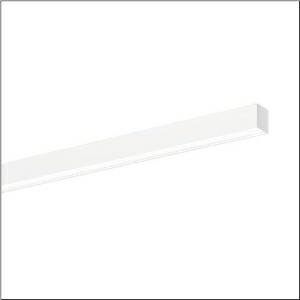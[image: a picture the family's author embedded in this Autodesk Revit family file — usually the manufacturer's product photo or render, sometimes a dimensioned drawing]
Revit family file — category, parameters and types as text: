
# Revit family: silica_r__21_51mx23db35wb_106f
name_source: partatom
category: Lighting Fixtures
units: mm (PartAtom-declared; Revit-internal decimal feet)

## family parameters
Cut with Voids When Loaded = No
Host = Face
Light Source = No
Part Type = Normal
Room Calculation Point = No
Round Connector Dimension = Use Diameter
Shared = No

## types (1)
- --- (1 x LED, 4100 lm, 30.1 W, 3000K)
    Apparent Load = 30 VA
    CIE Flux Codes = 78 96 99 100 100
    Color Rendering = 80
    Color Temperature = 3000K
    Default Elevation = 1800 mm
    Description = Silica® 21, office luminaire, primary optical cover: prismatic diffuser, of PMMA, CAT 2 (L<= 3000cd/m²), light emission: direct distribution, primary light characteristic: symmetric, installation type: surface-mounted, LED, rated luminous flux: 4.100lm, luminous efficacy: 136lm/W, light colour: 830, colour temperature: 3000K, control gear: DALI 2, with terminal, 3+2-pole, max. 2.5mm², mains connection: 220..240V, AC, 50/60Hz, rated input power: 30.1W, luminaire housing, of aluminium, traffic white (RAL 9016), length: 1.504mm, width: 53mm, height: 53mm, protection rating (complete): IP20, insulation class (complete): insulation class I (protective earthing), certification: CE, permissible operating ambient temperature: 0..+35°C, standard: EN 50419, packaging unit: 1 piece
    Height = 53 mm
    Lamp = 1 x LED
    Lamp Light Flux = 4100 lm
    Lamp Power = 30.1 W
    Lamp count = 1
    Length = 1504 mm
    Luminous efficacy = 136 lm/W
    Manufacturer = Siteco
    ModVariant = No
    Model = 51MX23DB35WB
    Mounting Place = Ceiling
    Mounting Type = Surface mounted
    Number of Poles = 1
    OnlyDefault = Yes
    Power Factor = 1
    Product Name = Silica® 21
    Product group = office luminaire | ceiling mounted
    ProductGroupID = 302
    Protection Class = Protection class I
    Protection Degree = IP 20
    RLX_Detail_Level = 1
    RLX_Emergency_Light_Flux = 0 lm
    RLX_Emergency_Type = 0
    RLX_Emergency_Type_DB = No
    RlxData = <blob elided: 18885 chars, md5=86baf039>
    Socket = socket
    Standby Power = 0 W
    System Light Flux = 4100 lm
    System Power = 30 W
    Type Comments = factory setting: luminous flux: 100 % | dim-lin: 254 | 345 mA
    Type Image = l_1335877.jpg
    URL = http://relux.com
    VarID = @adj_119548
    Voltage = 0 V
    Weight = 0.00 kg
    Width = 53 mm

## geometry (parser evidence)
native form markers: Blend x4, Sweep x12
no freeform markers — native parametric forms only
